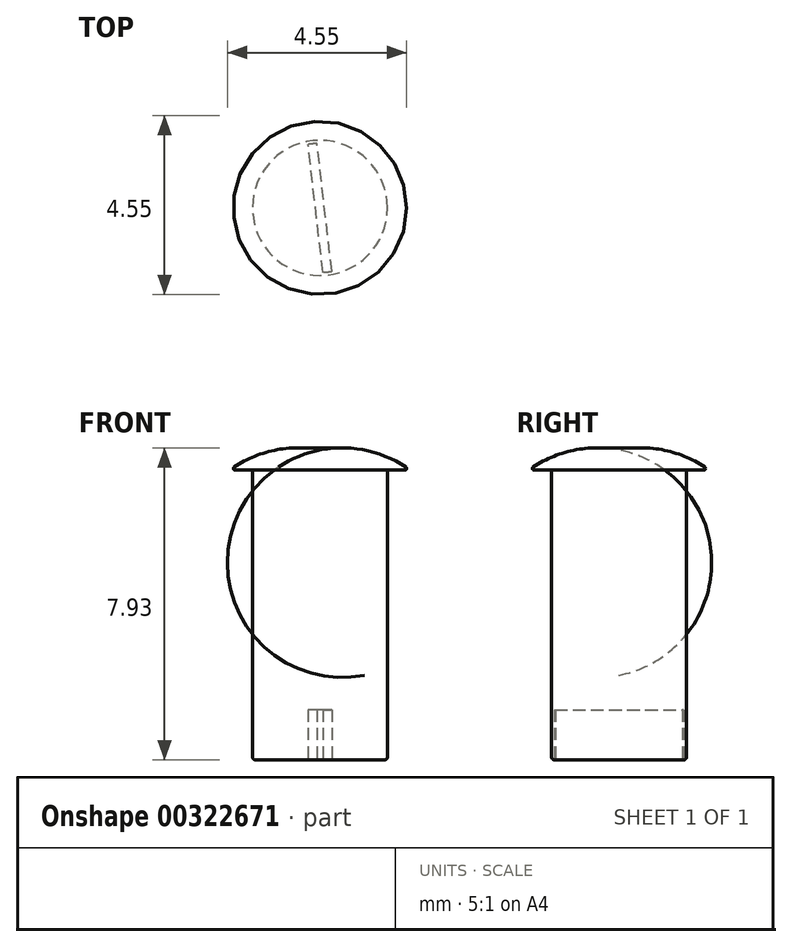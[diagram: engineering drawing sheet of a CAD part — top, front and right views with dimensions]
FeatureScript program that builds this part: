
annotation { "Feature Type Name" : "Feature", "Feature Type Description" : "" }
export const myFeature = defineFeature(function(context is Context, id is Id, definition is map)
    precondition{}
    {
        {
            var Q0;
            Q0=qCreatedBy(makeId("Front.planeOp"),FACE);
            var sketch = newSketch(context, id + "F0", { "sketchPlane" : qUnion([Q0])});
            skLineSegment(sketch, "E0", {"start": v(-31.44, -2.69) * mm, "end": v(-31.44, -9.98) * mm});
            skLineSegment(sketch, "E1", {"start": v(-31.37, -10.06) * mm, "end": v(-29.73, -10.06) * mm});
            skLineSegment(sketch, "E2", {"start": v(-31.44, -2.69) * mm, "end": v(-29.73, -2.69) * mm});
            skLineSegment(sketch, "E3", {"start": v(-29.73, -2.69) * mm, "end": v(-29.73, -10.06) * mm});
            skLineSegment(sketch, "E4", {"start": v(-29.73, -2.69) * mm, "end": v(-31.9, -2.69) * mm});
            skLineSegment(sketch, "E5", {"start": v(-29.73, -2.69) * mm, "end": v(-29.73, -2.18) * mm});
            skArc(sketch, "E6", {"start": v(-29.73, -2.18) * mm, "mid": v(-30.86, -2.18) * mm, "end": v(-31.91, -2.62) * mm});
            skPoint(sketch, "E7.visualSharp", {"position": v(-32.01, -2.69) * mm});
            skArc(sketch, "E7.filletArc", {"start": v(-31.91, -2.62) * mm, "mid": v(-31.93, -2.66) * mm, "end": v(-31.9, -2.69) * mm});
            skPoint(sketch, "E8.visualSharp", {"position": v(-31.44, -10.06) * mm});
            skArc(sketch, "E8.filletArc", {"start": v(-31.44, -9.98) * mm, "mid": v(-31.42, -10.03) * mm, "end": v(-31.37, -10.06) * mm});
            skSolve(sketch);
        }
        {
            var Q0;
            Q0 = qSketchRegion(id + "F0", true);
            var Q1;
            Q1=sQuery(id+"F0.wireOp",EDGE,"E3");
            revolve(context, id + "F1", {"entities" : qUnion([Q0]), "axis" : qUnion([Q1]), "revolveType" : RevolveType.FULL});
        }
        {
            var Q0;
            Q0=makeQuery(id+"F1.opRevolve","SWEPT_FACE",FACE,{"disambiguationData":[OSD([sQuery(id+"F0.wireOp",EDGE,"E1")])]});
            var sketch = newSketch(context, id + "F2", { "sketchPlane" : qUnion([Q0])});
            skCircle(sketch, "E9.0", {"center": v(-29.73, 0) * mm, "radius": 1.71 * mm});
            skLineSegment(sketch, "E10", {"start": v(-29.64, 1.71) * mm, "end": v(-30.04, -1.69) * mm});
            skLineSegment(sketch, "E11", {"start": v(-29.42, 1.69) * mm, "end": v(-29.81, -1.71) * mm});
            skArc(sketch, "E12", {"start": v(-29.42, 1.69) * mm, "mid": v(-29.53, 1.7) * mm, "end": v(-29.64, 1.71) * mm});
            skArc(sketch, "E13", {"start": v(-30.04, -1.69) * mm, "mid": v(-29.93, -1.7) * mm, "end": v(-29.81, -1.71) * mm});
            skSolve(sketch);
        }
        {
            var Q0;
            {var subQ0=sQuery(id+"F2.wireOp",EDGE,"E10");var subQ1=makeQuery(id+"F1.opRevolve","SWEPT_EDGE",EDGE,{"disambiguationData":[OSD([sQuery(id+"F0.wireOp",EDGE,"E1"),sQuery(id+"F0.wireOp",EDGE,"E8.filletArc")])]});var subQ2=makeQuery(id+"F2.imprint","INTERSECT",VERTEX,{"disambiguationData":[OD(0.0)],"derivedFrom":[subQ1,subQ0]});Q0=makeQuery(id+"F2.imprint","IMPRINT",FACE,{"disambiguationData":[TD([[makeQuery(id+"F2.imprint","IMPRINT",EDGE,{"disambiguationData":[TD([[subQ2,-1.0]])],"derivedFrom":subQ0}),1.0]])]});}
            extrude(context, id + "F3", {"entities" : qUnion([Q0]), "operationType" : NewBodyOperationType.REMOVE, "oppositeDirection" : true, "depth" : 1.27 * mm});
        }
    });
